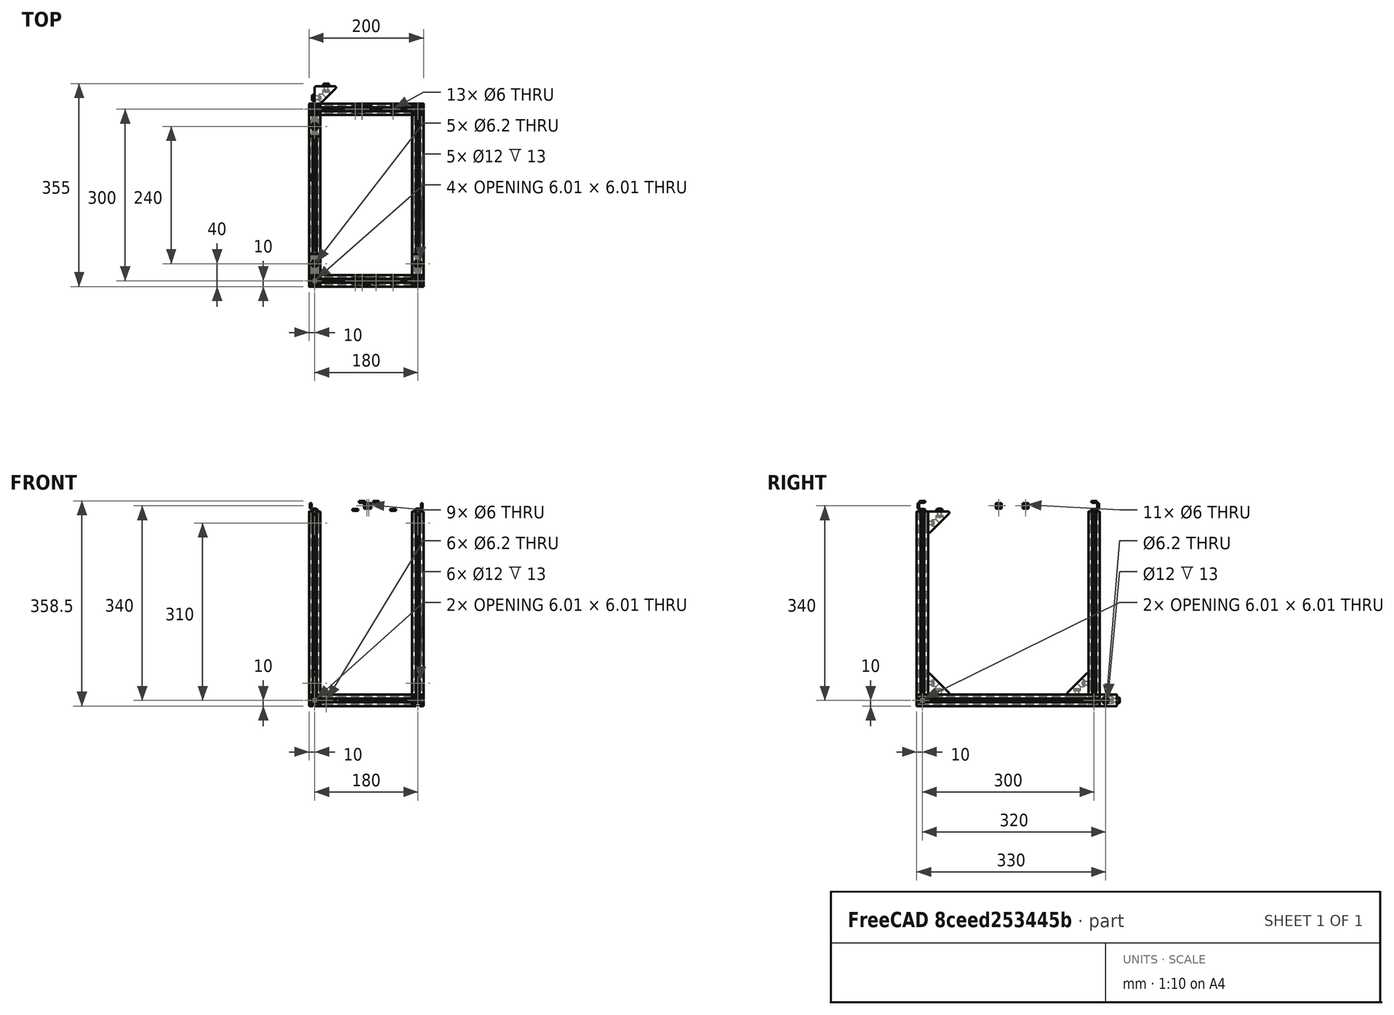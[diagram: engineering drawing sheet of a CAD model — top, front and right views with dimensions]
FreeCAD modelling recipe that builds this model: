
FCSTD DOCUMENT  (FreeCAD 0.17R9796 (Git))
Label: rawframe1
License: All rights reserved
LicenseURL: http://en.wikipedia.org/wiki/All_rights_reserved
objects: Part::Feature×63, Part::FeaturePython×16, App::Part×6, Part::Compound×5
note: 84 computed .brp shape members not serialized (recipe doc carries the construction recipe); baked Part::Feature solids carry a one-line shape summary decoded from their .brp

FEATURE [Part::Feature] Pocket003001  label="tslot32con"
  Placement = pos=(0,10,10) rot=(1,0,0;1.5708rad)
  shape: bbox 20 x 320 x 20 mm, 150 faces (baked)
FEATURE [Part::Feature] Pocket003002  label="tslot16"
  Placement = pos=(10,0,10) rot=(0,1,0;1.5708rad)
  shape: bbox 160 x 20 x 20 mm, 94 faces (baked)
FEATURE [Part::Feature] Pocket003006  label="tslot16_001"
  Placement = pos=(10,-300,10) rot=(0,1,0;1.5708rad)
  shape: bbox 160 x 20 x 20 mm, 94 faces (baked)
FEATURE [Part::Feature] Pocket003007  label="tslot32con_001"
  Placement = pos=(180,-310,10) rot=(0,0.707107,0.707107;3.14159rad)
  shape: bbox 20 x 320 x 20 mm, 150 faces (baked)
FEATURE [Part::FeaturePython] Screw  label="M6x25-Screw"  # Fasteners workbench fastener (typed FeaturePython)
  Placement = pos=(-4,0,10) rot=(0,-1,0;1.5708rad)
  diameter = 7
  invert = false
  length = 6
  matchOuter = false
  offset = 0
  thread = false
  type = 15
FEATURE [Part::FeaturePython] Screw001  label="M6x25-Screw004"  # Fasteners workbench fastener (typed FeaturePython)
  Placement = pos=(-4,-300,10) rot=(0,-1,0;1.5708rad)
  diameter = 7
  invert = false
  length = 6
  matchOuter = false
  offset = 0
  thread = false
  type = 15
FEATURE [Part::FeaturePython] Screw002  label="M6x25-Screw005"  # Fasteners workbench fastener (typed FeaturePython)
  Placement = pos=(184,0,10) rot=(0,1,0;1.5708rad)
  diameter = 7
  invert = false
  length = 6
  matchOuter = false
  offset = 0
  thread = false
  type = 15
FEATURE [Part::FeaturePython] Screw004  label="M6x25-Screw006"  # Fasteners workbench fastener (typed FeaturePython)
  Placement = pos=(184,-300,10) rot=(0,1,0;1.5708rad)
  diameter = 7
  invert = false
  length = 6
  matchOuter = false
  offset = 0
  thread = false
  type = 15
FEATURE [App::Part] Part  label="lower_frame"
  Group = -> [Pocket003001,Pocket003002,Pocket003006,Pocket003007,Screw,Screw001,Screw002,Screw004]
  License = CC BY 3.0
  LicenseURL = http://creativecommons.org/licenses/by/3.0/
  Origin = -> PartOrigin
FEATURE [Part::Feature] Pocket003008  label="tslot32con001"
  Placement = pos=(0,10,10) rot=(1,0,0;1.5708rad)
  shape: bbox 20 x 320 x 20 mm, 150 faces (baked)
FEATURE [Part::Feature] Pocket003009  label="tslot041"
  Placement = pos=(10,0,10) rot=(0,1,0;1.5708rad)
  shape: bbox 160 x 20 x 20 mm, 94 faces (baked)
FEATURE [Part::Feature] Pocket003010  label="tslot16_002"
  Placement = pos=(10,-300,10) rot=(0,1,0;1.5708rad)
  shape: bbox 160 x 20 x 20 mm, 94 faces (baked)
FEATURE [Part::Feature] Pocket003011  label="tslot32con_002"
  Placement = pos=(180,-310,10) rot=(0,0.707107,0.707107;3.14159rad)
  shape: bbox 20 x 320 x 20 mm, 150 faces (baked)
FEATURE [Part::FeaturePython] Screw005  label="M6x25-Screw012"  # Fasteners workbench fastener (typed FeaturePython)
  Placement = pos=(-4,0,10) rot=(0,-1,0;1.5708rad)
  diameter = 7
  invert = false
  length = 6
  matchOuter = false
  offset = 0
  thread = false
  type = 15
FEATURE [Part::FeaturePython] Screw006  label="M6x25-Screw015"  # Fasteners workbench fastener (typed FeaturePython)
  Placement = pos=(-4,-300,10) rot=(0,-1,0;1.5708rad)
  diameter = 7
  invert = false
  length = 6
  matchOuter = false
  offset = 0
  thread = false
  type = 15
FEATURE [Part::FeaturePython] Screw007  label="M6x25-Screw017"  # Fasteners workbench fastener (typed FeaturePython)
  Placement = pos=(184,0,10) rot=(0,1,0;1.5708rad)
  diameter = 7
  invert = false
  length = 6
  matchOuter = false
  offset = 0
  thread = false
  type = 15
FEATURE [Part::FeaturePython] Screw008  label="M6x25-Screw016"  # Fasteners workbench fastener (typed FeaturePython)
  Placement = pos=(184,-300,10) rot=(0,1,0;1.5708rad)
  diameter = 7
  invert = false
  length = 6
  matchOuter = false
  offset = 0
  thread = false
  type = 15
FEATURE [App::Part] Part001  label="upper_frame"
  Group = -> [Pocket003008,Pocket003009,Pocket003010,Pocket003011,Screw005,Screw006,Screw007,Screw008]
  License = CC BY 3.0
  LicenseURL = http://creativecommons.org/licenses/by/3.0/
  Origin = -> PartOrigin001
  Placement = pos=(0,0,340) rot=(0,0,1;0rad)
FEATURE [Part::Feature] Fillet004001  label="Fillet005"
  shape: bbox 37.5 x 37.5 x 20 mm, 26 faces (baked)
FEATURE [Part::FeaturePython] Screw009  label="M6x12-Screw"  # Fasteners workbench fastener (typed FeaturePython)
  Placement = pos=(7,20,10) rot=(0,1,0;1.5708rad)
  diameter = 4
  invert = false
  length = 1
  matchOuter = false
  offset = 0
  thread = false
  type = 20
FEATURE [Part::Feature] Body001  label="m6nutplate"
  Placement = pos=(-1.5,15,5) rot=(0,-1,0;1.5708rad)
  shape: bbox 3 x 10 x 10 mm, 9 faces (baked)
FEATURE [App::Part] Part002  label="cornerstonescrewnut"
  License = CC BY 3.0
  LicenseURL = http://creativecommons.org/licenses/by/3.0/
  Origin = -> PartOrigin002
  Placement = pos=(10,-50,20) rot=(0,-1,0;1.5708rad)
FEATURE [Part::FeaturePython] Screw010  label="M6x12-Screw001"  # Fasteners workbench fastener (typed FeaturePython)
  Placement = pos=(20,33,10) rot=(1,0,0;1.5708rad)
  diameter = 4
  invert = false
  length = 1
  matchOuter = false
  offset = 0
  thread = false
  type = 20
FEATURE [Part::Feature] Body002  label="m6nutplate001"
  Placement = pos=(15,41.5,5) rot=(0.57735,0.57735,0.57735;4.18879rad)
  shape: bbox 10 x 3 x 10 mm, 9 faces (baked)
FEATURE [Part::Feature] Fillet004002  label="Fillet006"
  shape: bbox 37.5 x 37.5 x 20 mm, 26 faces (baked)
FEATURE [Part::FeaturePython] Screw011  label="M6x12-Screw002"  # Fasteners workbench fastener (typed FeaturePython)
  Placement = pos=(7,20,10) rot=(0,1,0;1.5708rad)
  diameter = 4
  invert = false
  length = 1
  matchOuter = false
  offset = 0
  thread = false
  type = 20
FEATURE [Part::Feature] Body003  label="m6nutplate002"
  Placement = pos=(-1.5,15,5) rot=(0,-1,0;1.5708rad)
  shape: bbox 3 x 10 x 10 mm, 9 faces (baked)
FEATURE [Part::FeaturePython] Screw012  label="M6x12-Screw003"  # Fasteners workbench fastener (typed FeaturePython)
  Placement = pos=(20,33,10) rot=(1,0,0;1.5708rad)
  diameter = 4
  invert = false
  length = 1
  matchOuter = false
  offset = 0
  thread = false
  type = 20
FEATURE [Part::Feature] Body004  label="m6nutplate003"
  Placement = pos=(15,41.5,5) rot=(0.57735,0.57735,0.57735;4.18879rad)
  shape: bbox 10 x 3 x 10 mm, 9 faces (baked)
FEATURE [App::Part] Part003  label="cornerstonescrewnut001"
  Group = -> [Body003,Screw011,Fillet004002,Screw012,Body004,PartOrigin002,Body001,Screw009,Fillet004001,Screw010,Body002,Part002]
  License = CC BY 3.0
  LicenseURL = http://creativecommons.org/licenses/by/3.0/
  Origin = -> PartOrigin003
  Placement = pos=(190,-50,20) rot=(0,-1,0;1.5708rad)
FEATURE [Part::Feature] Fillet004003  label="Fillet007"
  shape: bbox 37.5 x 37.5 x 20 mm, 26 faces (baked)
FEATURE [Part::FeaturePython] Screw013  label="M6x12-Screw004"  # Fasteners workbench fastener (typed FeaturePython)
  Placement = pos=(7,20,10) rot=(0,1,0;1.5708rad)
  diameter = 4
  invert = false
  length = 1
  matchOuter = false
  offset = 0
  thread = false
  type = 20
FEATURE [Part::Feature] Body005  label="m6nutplate004"
  Placement = pos=(-1.5,15,5) rot=(0,-1,0;1.5708rad)
  shape: bbox 3 x 10 x 10 mm, 9 faces (baked)
FEATURE [Part::FeaturePython] Screw014  label="M6x12-Screw005"  # Fasteners workbench fastener (typed FeaturePython)
  Placement = pos=(20,33,10) rot=(1,0,0;1.5708rad)
  diameter = 4
  invert = false
  length = 1
  matchOuter = false
  offset = 0
  thread = false
  type = 20
FEATURE [Part::Feature] Body006  label="m6nutplate005"
  Placement = pos=(15,41.5,5) rot=(0.57735,0.57735,0.57735;4.18879rad)
  shape: bbox 10 x 3 x 10 mm, 9 faces (baked)
FEATURE [App::Part] Part004  label="cornerstonescrewnut002"
  Group = -> [Body005,Screw013,Fillet004003,Screw014,Body006]
  License = CC BY 3.0
  LicenseURL = http://creativecommons.org/licenses/by/3.0/
  Origin = -> PartOrigin004
  Placement = pos=(-10,-50,340) rot=(0,1,0;1.5708rad)
FEATURE [Part::Feature] Fillet004004  label="Fillet008"
  shape: bbox 37.5 x 37.5 x 20 mm, 26 faces (baked)
FEATURE [Part::FeaturePython] Screw015  label="M6x12-Screw006"  # Fasteners workbench fastener (typed FeaturePython)
  Placement = pos=(7,20,10) rot=(0,1,0;1.5708rad)
  diameter = 4
  invert = false
  length = 1
  matchOuter = false
  offset = 0
  thread = false
  type = 20
FEATURE [Part::Feature] Body007  label="m6nutplate006"
  Placement = pos=(-1.5,15,5) rot=(0,-1,0;1.5708rad)
  shape: bbox 3 x 10 x 10 mm, 9 faces (baked)
FEATURE [Part::FeaturePython] Screw016  label="M6x12-Screw007"  # Fasteners workbench fastener (typed FeaturePython)
  Placement = pos=(20,33,10) rot=(1,0,0;1.5708rad)
  diameter = 4
  invert = false
  length = 1
  matchOuter = false
  offset = 0
  thread = false
  type = 20
FEATURE [Part::Feature] Body008  label="m6nutplate007"
  Placement = pos=(15,41.5,5) rot=(0.57735,0.57735,0.57735;4.18879rad)
  shape: bbox 10 x 3 x 10 mm, 9 faces (baked)
FEATURE [App::Part] Part005  label="cornerstonescrewnut003"
  Group = -> [Body007,Screw015,Fillet004004,Screw016,Body008]
  License = CC BY 3.0
  LicenseURL = http://creativecommons.org/licenses/by/3.0/
  Origin = -> PartOrigin005
  Placement = pos=(170,-50,340) rot=(0,1,0;1.5708rad)
FEATURE [Part::Feature] Body009001  label="m6nutplate010"
  Placement = pos=(-1.5,15,5) rot=(0,-1,0;1.5708rad)
  shape: bbox 3 x 10 x 10 mm, 9 faces (baked)
FEATURE [Part::Feature] Body010001  label="m6nutplate011"
  Placement = pos=(15,41.5,5) rot=(0.57735,0.57735,0.57735;4.18879rad)
  shape: bbox 10 x 3 x 10 mm, 9 faces (baked)
FEATURE [Part::Feature] Screw018001  label="M6x12-Screw010"
  Placement = pos=(20,33,10) rot=(1,0,0;1.5708rad)
  shape: bbox 10.5 x 15.3 x 10.5 mm, 15 faces (baked)
FEATURE [Part::Feature] Screw017001  label="M6x12-Screw011"
  Placement = pos=(7,20,10) rot=(0,1,0;1.5708rad)
  shape: bbox 15.3 x 10.5 x 10.5 mm, 15 faces (baked)
FEATURE [Part::Feature] Fillet004005001  label="Fillet010"
  shape: bbox 37.5 x 37.5 x 20 mm, 26 faces (baked)
FEATURE [Part::Compound] Compound
  Links = -> [Body009001,Fillet004005001,Screw017001,Body010001,Screw018001]
  Placement = pos=(10,-250,340) rot=(0.707107,0,-0.707107;3.14159rad)
FEATURE [Part::Feature] Body010002  label="m6nutplate012"
  Placement = pos=(-1.5,15,5) rot=(0,-1,0;1.5708rad)
  shape: bbox 3 x 10 x 10 mm, 9 faces (baked)
FEATURE [Part::Feature] Body010003  label="m6nutplate013"
  Placement = pos=(15,41.5,5) rot=(0.57735,0.57735,0.57735;4.18879rad)
  shape: bbox 10 x 3 x 10 mm, 9 faces (baked)
FEATURE [Part::Feature] Screw018002  label="M6x12-Screw012"
  Placement = pos=(20,33,10) rot=(1,0,0;1.5708rad)
  shape: bbox 10.5 x 15.3 x 10.5 mm, 15 faces (baked)
FEATURE [Part::Feature] Screw018003  label="M6x12-Screw013"
  Placement = pos=(7,20,10) rot=(0,1,0;1.5708rad)
  shape: bbox 15.3 x 10.5 x 10.5 mm, 15 faces (baked)
FEATURE [Part::Feature] Fillet004005002  label="Fillet011"
  shape: bbox 37.5 x 37.5 x 20 mm, 26 faces (baked)
FEATURE [Part::Compound] Compound001
  Links = -> [Body010002,Fillet004005002,Screw018003,Body010003,Screw018002]
  Placement = pos=(190,-250,340) rot=(0.707107,0,-0.707107;3.14159rad)
FEATURE [Part::Feature] Body010004  label="m6nutplate014"
  Placement = pos=(-1.5,15,5) rot=(0,-1,0;1.5708rad)
  shape: bbox 3 x 10 x 10 mm, 9 faces (baked)
FEATURE [Part::Feature] Body010005  label="m6nutplate015"
  Placement = pos=(15,41.5,5) rot=(0.57735,0.57735,0.57735;4.18879rad)
  shape: bbox 10 x 3 x 10 mm, 9 faces (baked)
FEATURE [Part::Feature] Screw018004  label="M6x12-Screw014"
  Placement = pos=(20,33,10) rot=(1,0,0;1.5708rad)
  shape: bbox 10.5 x 15.3 x 10.5 mm, 15 faces (baked)
FEATURE [Part::Feature] Screw018005  label="M6x12-Screw015"
  Placement = pos=(7,20,10) rot=(0,1,0;1.5708rad)
  shape: bbox 15.3 x 10.5 x 10.5 mm, 15 faces (baked)
FEATURE [Part::Feature] Fillet004005003  label="Fillet012"
  shape: bbox 37.5 x 37.5 x 20 mm, 26 faces (baked)
FEATURE [Part::Compound] Compound002
  Links = -> [Body010004,Fillet004005003,Screw018005,Body010005,Screw018004]
  Placement = pos=(10,-290,60) rot=(0.57735,0.57735,-0.57735;4.18879rad)
FEATURE [Part::Feature] Body010006  label="m6nutplate016"
  Placement = pos=(-1.5,15,5) rot=(0,-1,0;1.5708rad)
  shape: bbox 3 x 10 x 10 mm, 9 faces (baked)
FEATURE [Part::Feature] Body010007  label="m6nutplate017"
  Placement = pos=(15,41.5,5) rot=(0.57735,0.57735,0.57735;4.18879rad)
  shape: bbox 10 x 3 x 10 mm, 9 faces (baked)
FEATURE [Part::Feature] Screw018006  label="M6x12-Screw016"
  Placement = pos=(20,33,10) rot=(1,0,0;1.5708rad)
  shape: bbox 10.5 x 15.3 x 10.5 mm, 15 faces (baked)
FEATURE [Part::Feature] Screw018007  label="M6x12-Screw017"
  Placement = pos=(7,20,10) rot=(0,1,0;1.5708rad)
  shape: bbox 15.3 x 10.5 x 10.5 mm, 15 faces (baked)
FEATURE [Part::Feature] Fillet004005004  label="Fillet013"
  shape: bbox 37.5 x 37.5 x 20 mm, 26 faces (baked)
FEATURE [Part::Compound] Compound003
  Links = -> [Body010006,Fillet004005004,Screw018007,Body010007,Screw018006]
  Placement = pos=(190,-290,60) rot=(0.57735,0.57735,-0.57735;4.18879rad)
FEATURE [Part::Feature] Pocket001001  label="tslot32"
  Placement = pos=(0,0,20) rot=(0,0,1;0rad)
  shape: bbox 20 x 20 x 320 mm, 94 faces (baked)
FEATURE [Part::Feature] Body010008  label="m6nutplate018"
  Placement = pos=(-1.5,15,5) rot=(0,-1,0;1.5708rad)
  shape: bbox 3 x 10 x 10 mm, 9 faces (baked)
FEATURE [Part::Feature] Body010009  label="m6nutplate019"
  Placement = pos=(15,41.5,5) rot=(0.57735,0.57735,0.57735;4.18879rad)
  shape: bbox 10 x 3 x 10 mm, 9 faces (baked)
FEATURE [Part::Feature] Screw018008  label="M6x12-Screw018"
  Placement = pos=(20,33,10) rot=(1,0,0;1.5708rad)
  shape: bbox 10.5 x 15.3 x 10.5 mm, 15 faces (baked)
FEATURE [Part::Feature] Screw018009  label="M6x12-Screw019"
  Placement = pos=(7,20,10) rot=(0,1,0;1.5708rad)
  shape: bbox 15.3 x 10.5 x 10.5 mm, 15 faces (baked)
FEATURE [Part::Feature] Fillet004005005  label="Fillet014"
  shape: bbox 37.5 x 37.5 x 20 mm, 26 faces (baked)
FEATURE [Part::Compound] Compound004
  Links = -> [Body010008,Fillet004005005,Screw018009,Body010009,Screw018008]
  Placement = pos=(-10,-10,60) rot=(0.57735,-0.57735,0.57735;4.18879rad)
FEATURE [Part::Feature] Pocket003012  label="tslot32_001"
  Placement = pos=(0,-300,20) rot=(0,0,1;0rad)
  shape: bbox 20 x 20 x 320 mm, 94 faces (baked)
FEATURE [Part::Feature] Pocket003013  label="tslot32_002"
  Placement = pos=(180,0,20) rot=(0,0,1;0rad)
  shape: bbox 20 x 20 x 320 mm, 94 faces (baked)
FEATURE [Part::Feature] Pocket003014  label="tslot32_003"
  Placement = pos=(180,-300,20) rot=(0,0,1;0rad)
  shape: bbox 20 x 20 x 320 mm, 94 faces (baked)
FEATURE [Part::Feature] Chamfer001001  label="m6nutplate020uf"
  Placement = pos=(112,-295,358.5) rot=(0.707107,-0.707107,0;3.14159rad)
  shape: bbox 10 x 10 x 3 mm, 9 faces (baked)
FEATURE [Part::Feature] Chamfer001002  label="m6nutplate021lf"
  Placement = pos=(96,-308.5,355) rot=(0.57735,-0.57735,-0.57735;4.18879rad)
  shape: bbox 10 x 3 x 10 mm, 9 faces (baked)
FEATURE [Part::Feature] Chamfer001003  label="m6nutplate022lf"
  Placement = pos=(-8.5,-124.5,355) rot=(0,1,0;1.5708rad)
  shape: bbox 3 x 10 x 10 mm, 9 faces (baked)
FEATURE [Part::Feature] Chamfer001004  label="m6nutplate023lf"
  Placement = pos=(88,5,358.5) rot=(0.707107,-0.707107,0;3.14159rad)
  shape: bbox 10 x 10 x 3 mm, 9 faces (baked)
FEATURE [Part::Feature] Chamfer001005  label="m6nutplate024lf"
  Placement = pos=(96,8.5,345) rot=(0.57735,-0.57735,0.57735;2.0944rad)
  shape: bbox 10 x 3 x 10 mm, 9 faces (baked)
FEATURE [Part::Feature] Chamfer001006  label="m6nutplate025lf"
  Placement = pos=(188.5,-171.5,345) rot=(0,-1,0;1.5708rad)
  shape: bbox 3 x 10 x 10 mm, 9 faces (baked)
FEATURE [Part::Feature] Chamfer001007  label="m6nutplate026lf"
  Placement = pos=(88,-295,358.5) rot=(0.707107,-0.707107,0;3.14159rad)
  shape: bbox 10 x 10 x 3 mm, 9 faces (baked)
FEATURE [Part::Feature] Chamfer001008  label="m6nutplate027lf"
  Placement = pos=(142,-5,341.6) rot=(0,0,1;1.5708rad)
  shape: bbox 10 x 10 x 3 mm, 9 faces (baked)
FEATURE [Part::Feature] Chamfer001009  label="m6nutplate028uf"
  Placement = pos=(96,-308.5,355) rot=(0.57735,-0.57735,-0.57735;4.18879rad)
  shape: bbox 10 x 3 x 10 mm, 9 faces (baked)
FEATURE [Part::Feature] Chamfer001010  label="m6nutplate029uf"
  Placement = pos=(87,5,358.5) rot=(0.707107,-0.707107,0;3.14159rad)
  shape: bbox 10 x 10 x 3 mm, 9 faces (baked)
FEATURE [Part::Feature] Chamfer001011  label="m6nutplate030lf"
  Placement = pos=(142,-305,341.6) rot=(0,0,1;1.5708rad)
  shape: bbox 10 x 10 x 3 mm, 9 faces (baked)
FEATURE [Part::Feature] Chamfer001012  label="m6nutplate031lf"
  Placement = pos=(76,-5,341.6) rot=(0,0,1;1.5708rad)
  shape: bbox 10 x 10 x 3 mm, 9 faces (baked)
FEATURE [Part::Feature] Chamfer001013  label="m6nutplate032uf"
  Placement = pos=(99,8.4,345) rot=(0.57735,-0.57735,0.57735;2.0944rad)
  shape: bbox 10 x 3 x 10 mm, 9 faces (baked)
FEATURE [Part::Feature] Chamfer001014  label="m6nutplate033lf"
  Placement = pos=(76,-305,341.6) rot=(0,0,1;1.5708rad)
  shape: bbox 10 x 10 x 3 mm, 9 faces (baked)
